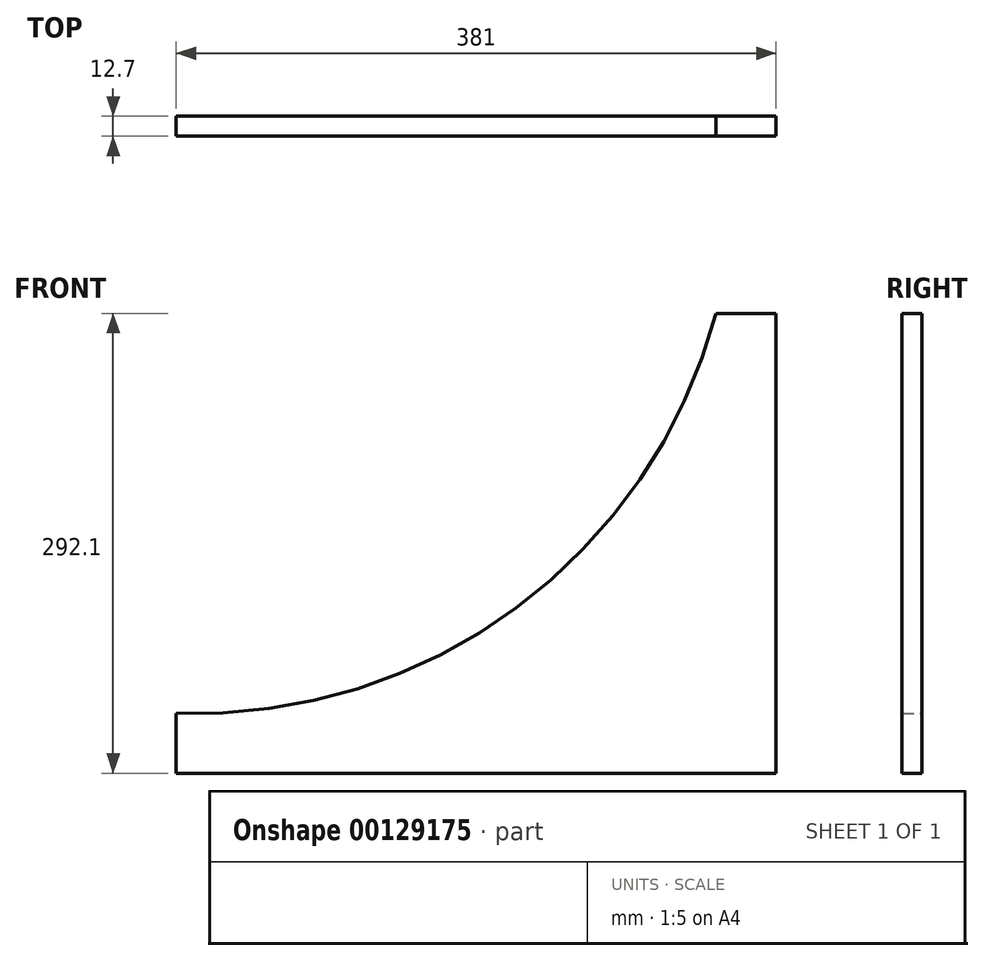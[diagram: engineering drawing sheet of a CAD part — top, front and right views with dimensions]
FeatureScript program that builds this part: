
annotation { "Feature Type Name" : "Feature", "Feature Type Description" : "" }
export const myFeature = defineFeature(function(context is Context, id is Id, definition is map)
    precondition{}
    {
        {
            var Q0;
            Q0=qCreatedBy(makeId("Front.planeOp"),FACE);
            var sketch = newSketch(context, id + "F0", { "sketchPlane" : qUnion([Q0])});
            skLineSegment(sketch, "E0.top", {"start": v(-190.5, -146.05) * mm, "end": v(190.5, -146.05) * mm});
            skLineSegment(sketch, "E0.right", {"start": v(190.5, 146.05) * mm, "end": v(190.5, -146.05) * mm});
            skPoint(sketch, "E0.middle", {"position": v(0, 0) * mm});
            skLineSegment(sketch, "E1", {"start": v(190.5, 146.05) * mm, "end": v(152.4, 146.05) * mm});
            skLineSegment(sketch, "E2", {"start": v(-190.5, -146.05) * mm, "end": v(-190.5, -107.95) * mm});
            skArc(sketch, "E3", {"start": v(-190.5, -107.95) * mm, "mid": v(25.44, -41) * mm, "end": v(152.4, 146.05) * mm});
            skSolve(sketch);
        }
        {
            var Q0;
            Q0 = qSketchRegion(id + "F0", true);
            extrude(context, id + "F1", {"entities" : qUnion([Q0]), "depth" : 12.7 * mm});
        }
    });
